# Revit family: 259519 Strømforsyning 24V 5A
name_source: partatom
category: Electrical Equipment
revit_build: Autodesk Revit 2016 (Build: 20160314_0715(x64)
units: mm (PartAtom-declared; Revit-internal decimal feet)

## family parameters
Always vertical = Yes
Cut with Voids When Loaded = No
OmniClass Number = 23.85.30.21.11
OmniClass Title = Fire Detection, Monitoring and Alarm
Part Type = Other Panel
Room Calculation Point = No
Round Connector Dimension = Use Diameter
Shared = No
Work Plane-Based = No

## types (1)
- Strømforsyning 230V/24V
    Assembly Code = 5422
    CQ Depth = 110 mm  [stored 0.360892 ft]
    CQ Display = Laminate, Grey
    CQ Font = 0 mm  [stored 0 ft]
    CQ Height = 404 mm  [stored 1.32546 ft]
    CQ Material = Laminate, White
    CQ Type = 24V
    CQ Type tekst synlig = Yes
    CQ Voltage = 230 V
    CQ Width = 400 mm  [stored 1.31234 ft]
    CQFontSymboler = t
    Keynote = WB3
    Manufacturer = Honeywell
    NS8360 = 5422_WB3
    Type Comments = -XG

note: [stored X ft] marks values corroborated as IEEE doubles in the binary element streams (Revit-internal decimal feet)

## geometry (parser evidence)
native form markers: Blend x3, Sweep x3
no freeform markers — native parametric forms only
